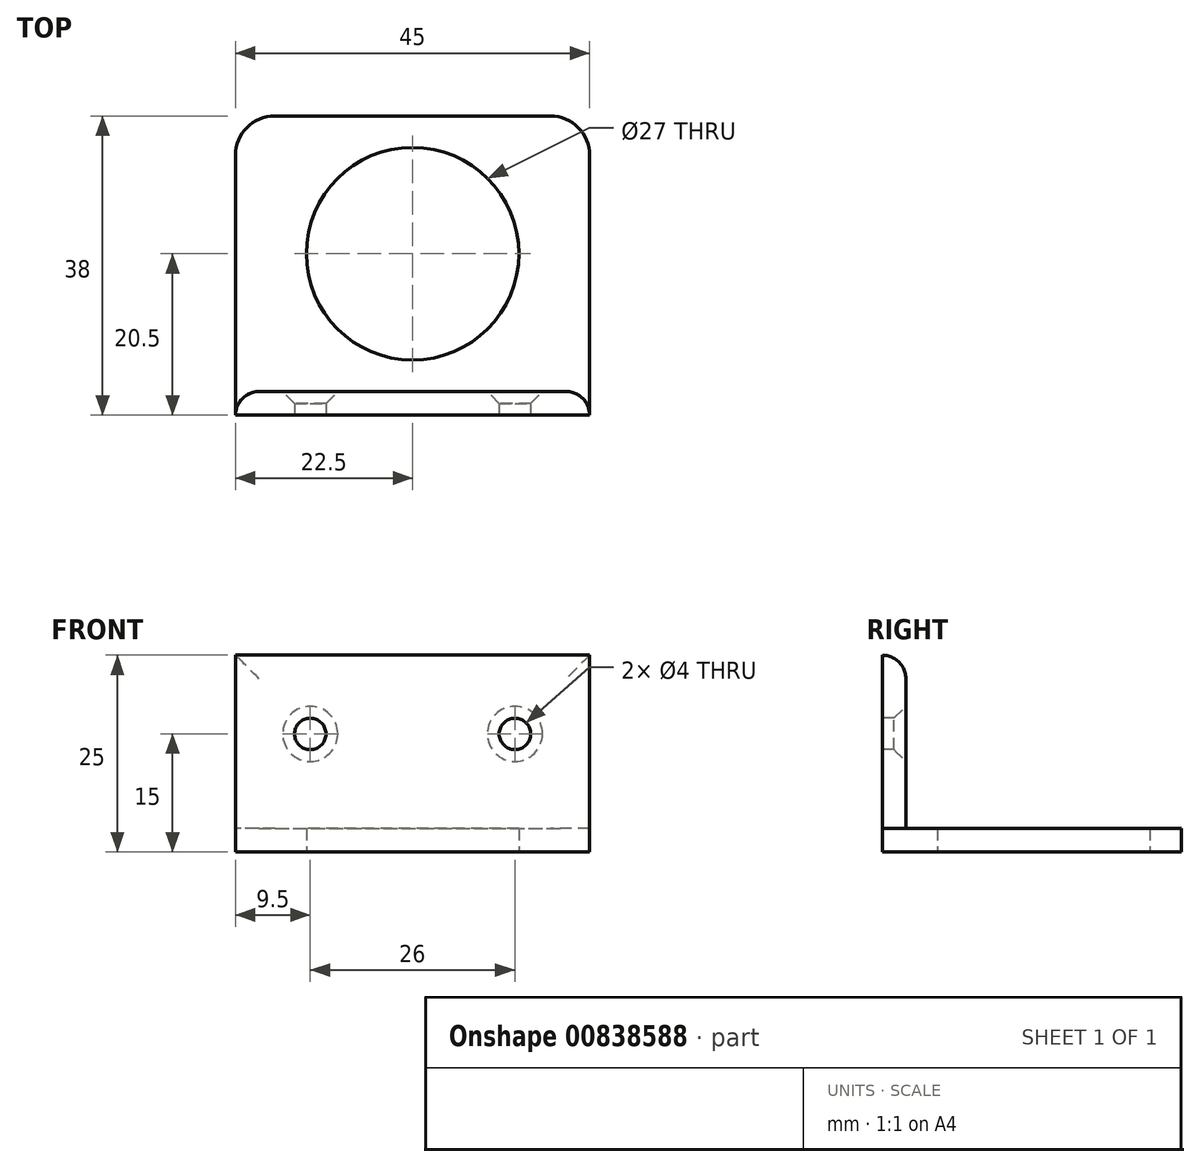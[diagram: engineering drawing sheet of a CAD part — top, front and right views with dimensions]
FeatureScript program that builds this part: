
annotation { "Feature Type Name" : "Feature", "Feature Type Description" : "" }
export const myFeature = defineFeature(function(context is Context, id is Id, definition is map)
    precondition{}
    {
        {
            var Q0;
            Q0=qCreatedBy(makeId("Top.planeOp"),FACE);
            var sketch = newSketch(context, id + "F0", { "sketchPlane" : qUnion([Q0])});
            skLineSegment(sketch, "E0.bottom", {"start": v(0, 0) * mm, "end": v(45, 0) * mm});
            skLineSegment(sketch, "E0.top", {"start": v(5, 38) * mm, "end": v(40, 38) * mm});
            skLineSegment(sketch, "E0.left", {"start": v(0, 0) * mm, "end": v(0, 33) * mm});
            skLineSegment(sketch, "E0.right", {"start": v(45, 0) * mm, "end": v(45, 33) * mm});
            skLineSegment(sketch, "E1.top", {"start": v(0, 3) * mm, "end": v(45, 3) * mm});
            skLineSegment(sketch, "E1.left", {"start": v(0, 0) * mm, "end": v(0, 3) * mm});
            skLineSegment(sketch, "E1.right", {"start": v(45, 0) * mm, "end": v(45, 3) * mm});
            skLineSegment(sketch, "E2", {"start": v(0, 20.5) * mm, "end": v(45, 20.5) * mm, "construction": true});
            skEllipse(sketch, "E3", {"center": v(22.5, 20.5) * mm, "majorRadius": 13.5 * mm, "minorRadius": 13.5 * mm, "majorAxis": v(1, 0)});
            skPoint(sketch, "E4.visualSharp", {"position": v(0, 38) * mm});
            skArc(sketch, "E4.filletArc", {"start": v(5, 38) * mm, "mid": v(1.46, 36.54) * mm, "end": v(0, 33) * mm});
            skPoint(sketch, "E5.visualSharp", {"position": v(45, 38) * mm});
            skArc(sketch, "E5.filletArc", {"start": v(45, 33) * mm, "mid": v(43.54, 36.54) * mm, "end": v(40, 38) * mm});
            skSolve(sketch);
        }
        {
            var Q0;
            Q0=makeQuery(id+"F0.imprint","IMPRINT",FACE,{"disambiguationData":[TD([[makeQuery(id+"F0.imprint","IMPRINT",EDGE,{"derivedFrom":sQuery(id+"F0.wireOp",EDGE,"E0.top")}),-1.0]])]});
            extrude(context, id + "F1", {"entities" : qUnion([Q0]), "flatOperationType" : FlatOperationType.REMOVE, "depth" : 3 * mm, "offsetDistance" : 25 * mm, "domain" : OperationDomain.MODEL});
        }
        {
            var Q0;
            {var subQ0=sQuery(id+"F0.wireOp",EDGE,"E0.bottom");Q0=makeQuery(id+"F0.imprint","IMPRINT",FACE,{"disambiguationData":[TD([[makeQuery(id+"F0.imprint","IMPRINT",EDGE,{"derivedFrom":subQ0}),1.0]])]});}
            extrude(context, id + "F2", {"entities" : qUnion([Q0]), "operationType" : NewBodyOperationType.ADD, "flatOperationType" : FlatOperationType.REMOVE, "depth" : 25 * mm, "offsetDistance" : 25 * mm, "domain" : OperationDomain.MODEL});
        }
        {
            var Q0;
            Q0=makeQuery(id+"F2.opExtrude","SWEPT_FACE",FACE,{"disambiguationData":[OSD([sQuery(id+"F0.wireOp",EDGE,"E1.top")])]});
            var sketch = newSketch(context, id + "F3", { "sketchPlane" : qUnion([Q0])});
            skLineSegment(sketch, "E6.0", {"start": v(-45, 25) * mm, "end": v(-45, 3) * mm});
            skLineSegment(sketch, "E7.0", {"start": v(0, 25) * mm, "end": v(-45, 25) * mm});
            skLineSegment(sketch, "E8.0", {"start": v(0, 25) * mm, "end": v(0, 3) * mm});
            skPoint(sketch, "E9.positionSnap0", {"position": v(-22.5, 25) * mm});
            skLineSegment(sketch, "E10", {"start": v(-35.5, 15) * mm, "end": v(-9.5, 15) * mm});
            skLineSegment(sketch, "E11", {"start": v(-35.5, 15) * mm, "end": v(-45, 15) * mm});
            skLineSegment(sketch, "E12", {"start": v(-9.5, 15) * mm, "end": v(0, 15) * mm});
            skSolve(sketch);
        }
        {
            var Q0;
            Q0=sQuery(id+"F3.wireOp",VERTEX,"E10.start");
            var Q1;
            Q1=sQuery(id+"F3.wireOp",VERTEX,"E10.end");
            var Q2;
            Q2=makeQuery(id+"F1.opExtrude","SWEPT_BODY",BODY,{"disambiguationData":[OSD([sQuery(id+"F0.wireOp",EDGE,"E0.top"),sQuery(id+"F0.wireOp",EDGE,"E0.left"),sQuery(id+"F0.wireOp",EDGE,"E0.right"),sQuery(id+"F0.wireOp",EDGE,"E1.top"),sQuery(id+"F0.wireOp",EDGE,"E3"),sQuery(id+"F0.wireOp",EDGE,"E4.filletArc"),sQuery(id+"F0.wireOp",EDGE,"E5.filletArc")])]});
            hole(context, id + "F4", {"style" : HoleStyle.C_SINK, "endStyle" : HoleEndStyle.THROUGH, "holeDiameter" : 4 * mm, "cSinkDiameter" : 7 * mm, "cSinkAngle" : 90 * degree, "majorDiameter" : 5 * mm, "isTappedThrough" : true, "tappedDepth" : 12 * mm, "tapClearance" : 3, "locations" : qUnion([Q0, Q1]), "scope" : qUnion([Q2]), "startStyle" : HoleStartStyle.PART});
        }
        {
            var Q0;
            Q0=makeQuery(id+"F2.opExtrude","SWEPT_EDGE",EDGE,{"disambiguationData":[OSD([sQuery(id+"F0.wireOp",EDGE,"E0.right"),sQuery(id+"F0.wireOp",EDGE,"E1.top")])]});
            var Q1;
            Q1=makeQuery(id+"F2.opExtrude","CAP_EDGE",EDGE,{"disambiguationData":[OSD([sQuery(id+"F0.wireOp",EDGE,"E1.top")])],"isStart":false});
            var Q2;
            Q2=makeQuery(id+"F2.opExtrude","SWEPT_EDGE",EDGE,{"disambiguationData":[OSD([sQuery(id+"F0.wireOp",EDGE,"E0.left"),sQuery(id+"F0.wireOp",EDGE,"E1.top")])]});
            fillet(context, id + "F5", {"entities" : qUnion([Q0, Q1, Q2]), "radius" : 3 * mm, "tangentPropagation" : true, "defaultsChanged" : false, "allowEdgeOverflow" : false, "vertexSettings" : [], "filletType" : FilletType.EDGE});
        }
    });
